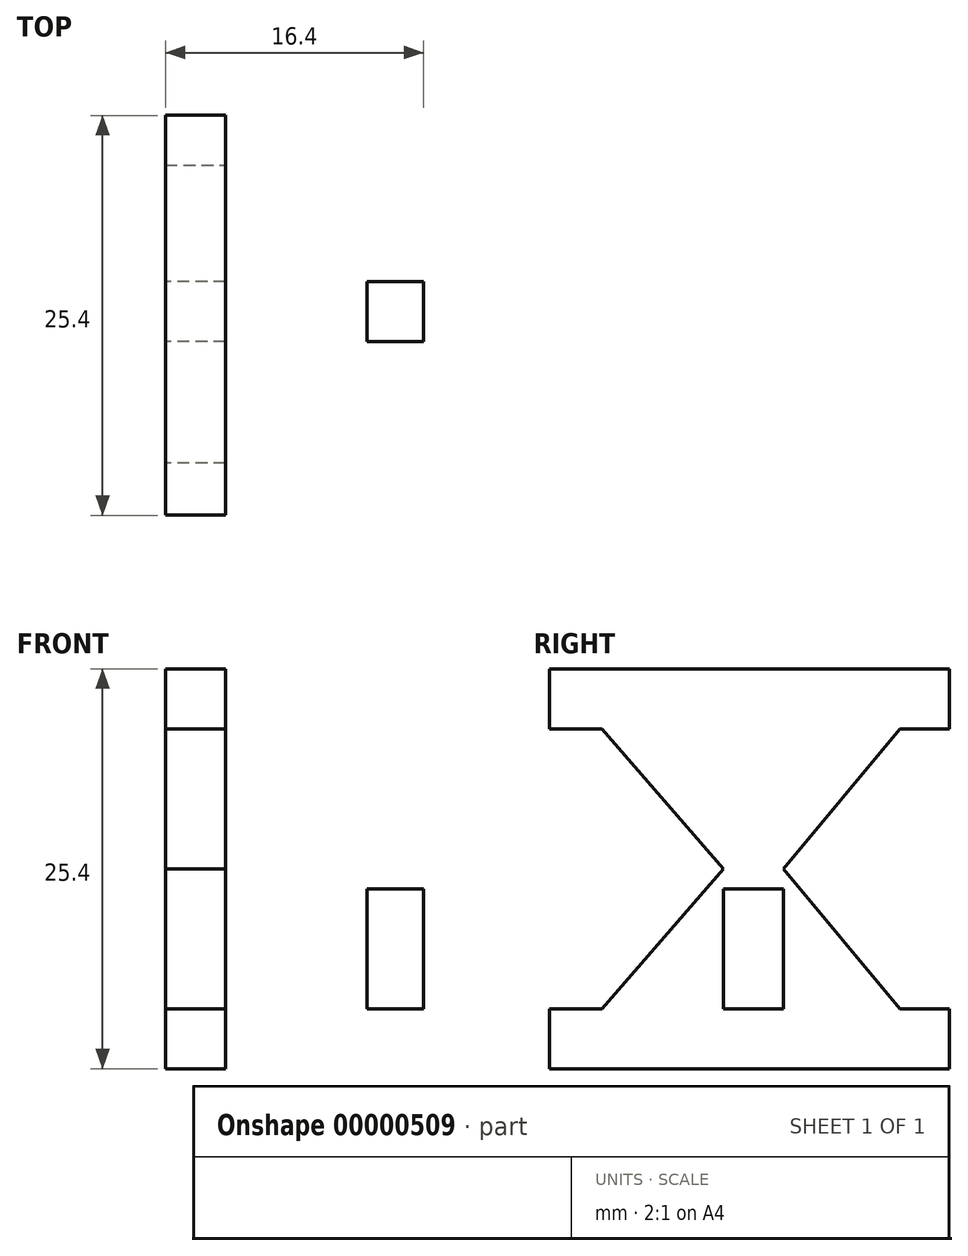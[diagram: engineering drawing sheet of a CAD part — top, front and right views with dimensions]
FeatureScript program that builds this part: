
annotation { "Feature Type Name" : "Feature", "Feature Type Description" : "" }
export const myFeature = defineFeature(function(context is Context, id is Id, definition is map)
    precondition{}
    {
        {
            var Q0;
            Q0=qCreatedBy(makeId("Top.planeOp"),FACE);
            var sketch = newSketch(context, id + "F0", { "sketchPlane" : qUnion([Q0])});
            skLineSegment(sketch, "E0.bottom", {"start": v(0, 12.45) * mm, "end": v(-3.81, 12.45) * mm});
            skLineSegment(sketch, "E0.top", {"start": v(0, -12.95) * mm, "end": v(-3.8, -12.95) * mm});
            skLineSegment(sketch, "E0.left", {"start": v(0, 12.45) * mm, "end": v(0, -12.95) * mm});
            skLineSegment(sketch, "E0.right", {"start": v(-3.81, 12.45) * mm, "end": v(-3.8, -12.95) * mm});
            skArc(sketch, "E1", {"start": v(0, -12.95) * mm, "mid": v(12.7, -0.25) * mm, "end": v(0, 12.45) * mm});
            skLineSegment(sketch, "E2", {"start": v(0, 12.45) * mm, "end": v(0, 8.64) * mm});
            skLineSegment(sketch, "E3", {"start": v(0, 8.64) * mm, "end": v(0, -9.14) * mm});
            skLineSegment(sketch, "E4", {"start": v(0, -9.14) * mm, "end": v(0, -12.95) * mm});
            skLineSegment(sketch, "E5", {"start": v(0, 0) * mm, "end": v(8.89, 0) * mm});
            skLineSegment(sketch, "E6", {"start": v(8.89, 0) * mm, "end": v(12.7, 0) * mm});
            skArc(sketch, "E7", {"start": v(0, -9.14) * mm, "mid": v(8.9, -0.25) * mm, "end": v(0, 8.64) * mm});
            skSolve(sketch);
        }
        {
            var Q0;
            Q0=makeQuery(id+"F0.imprint","IMPRINT",FACE,{"disambiguationData":[TD([[makeQuery(id+"F0.imprint","IMPRINT",EDGE,{"derivedFrom":sQuery(id+"F0.wireOp",EDGE,"E0.bottom")}),1.0]])]});
            var Q1;
            {var subQ2=sQuery(id+"F0.wireOp",EDGE,"E4");Q1=makeQuery(id+"F0.imprint","IMPRINT",FACE,{"disambiguationData":[TD([[makeQuery(id+"F0.imprint","IMPRINT",EDGE,{"derivedFrom":subQ2}),1.0]])]});}
            var Q2;
            {var subQ2=sQuery(id+"F0.wireOp",EDGE,"E2");Q2=makeQuery(id+"F0.imprint","IMPRINT",FACE,{"disambiguationData":[TD([[makeQuery(id+"F0.imprint","IMPRINT",EDGE,{"derivedFrom":subQ2}),1.0]])]});}
            extrude(context, id + "F1", {"entities" : qUnion([Q0, Q1, Q2]), "depth" : 3.8 * mm});
        }
        {
            var Q0;
            Q0=makeQuery(id+"F1.opExtrude","CAP_FACE",FACE,{"disambiguationData":[OSD([sQuery(id+"F0.wireOp",EDGE,"E0.bottom"),sQuery(id+"F0.wireOp",EDGE,"E0.top"),sQuery(id+"F0.wireOp",EDGE,"E0.right"),sQuery(id+"F0.wireOp",EDGE,"E1"),sQuery(id+"F0.wireOp",EDGE,"E3"),sQuery(id+"F0.wireOp",EDGE,"E7")])],"isStart":false});
            var sketch = newSketch(context, id + "F2", { "sketchPlane" : qUnion([Q0])});
            skLineSegment(sketch, "E8", {"start": v(0, 0) * mm, "end": v(-3.8, 0) * mm, "construction": true});
            skLineSegment(sketch, "E9.rect.bottom", {"start": v(-3.8, -1.9) * mm, "end": v(0, -1.9) * mm});
            skLineSegment(sketch, "E9.rect.top", {"start": v(-3.8, 1.9) * mm, "end": v(0, 1.9) * mm});
            skLineSegment(sketch, "E9.rect.left", {"start": v(-3.8, -1.9) * mm, "end": v(-3.8, 1.9) * mm});
            skLineSegment(sketch, "E9.rect.right", {"start": v(0, -1.9) * mm, "end": v(0, 1.9) * mm});
            skPoint(sketch, "E9.rect.middle", {"position": v(-1.9, 0) * mm});
            skSolve(sketch);
        }
        {
            var Q0;
            Q0 = qSketchRegion(id + "F2", true);
            extrude(context, id + "F3", {"entities" : qUnion([Q0]), "operationType" : NewBodyOperationType.ADD, "depth" : 25.4 * mm - 7.62 * mm});
        }
        {
            var Q0;
            Q0=makeQuery(id+"F1.opExtrude","CAP_FACE",FACE,{"disambiguationData":[OSD([sQuery(id+"F0.wireOp",EDGE,"E0.bottom"),sQuery(id+"F0.wireOp",EDGE,"E0.top"),sQuery(id+"F0.wireOp",EDGE,"E0.right"),sQuery(id+"F0.wireOp",EDGE,"E1"),sQuery(id+"F0.wireOp",EDGE,"E3"),sQuery(id+"F0.wireOp",EDGE,"E7")])],"isStart":false});
            var sketch = newSketch(context, id + "F4", { "sketchPlane" : qUnion([Q0])});
            skLineSegment(sketch, "E10", {"start": v(12.7, 0) * mm, "end": v(8.89, 0) * mm, "construction": true});
            skLineSegment(sketch, "E11.rect.bottom", {"start": v(12.6, -1.9) * mm, "end": v(9, -1.9) * mm});
            skLineSegment(sketch, "E11.rect.top", {"start": v(12.6, 1.9) * mm, "end": v(9, 1.9) * mm});
            skLineSegment(sketch, "E11.rect.left", {"start": v(12.6, -1.9) * mm, "end": v(12.6, 1.9) * mm});
            skLineSegment(sketch, "E11.rect.right", {"start": v(9, -1.9) * mm, "end": v(9, 1.9) * mm});
            skPoint(sketch, "E11.rect.middle", {"position": v(10.8, 0) * mm});
            skSolve(sketch);
        }
        {
            var Q0;
            Q0 = qSketchRegion(id + "F4", true);
            extrude(context, id + "F5", {"entities" : qUnion([Q0]), "operationType" : NewBodyOperationType.ADD, "depth" : 7.62 * mm});
        }
        {
            var Q0;
            Q0=makeQuery(id+"F3.opExtrude","CAP_FACE",FACE,{"disambiguationData":[OSD([sQuery(id+"F2.wireOp",EDGE,"E9.rect.bottom"),sQuery(id+"F2.wireOp",EDGE,"E9.rect.top"),sQuery(id+"F2.wireOp",EDGE,"E9.rect.left"),sQuery(id+"F2.wireOp",EDGE,"E9.rect.right")])],"isStart":false});
            extrude(context, id + "F6", {"entities" : qUnion([Q0]), "operationType" : NewBodyOperationType.ADD, "depth" : 3.8 * mm});
        }
        {
            var Q0;
            {var subQ0=sQuery(id+"F2.wireOp",EDGE,"E9.rect.bottom");Q0=makeQuery(id+"F6.boolean.opBoolean","MERGE",FACE,{"derivedFrom":[makeQuery(id+"F3.opExtrude","SWEPT_FACE",FACE,{"disambiguationData":[OSD([subQ0])]}),makeQuery(id+"F6.opExtrude","SWEPT_FACE",FACE,{"disambiguationData":[OSD([subQ0])]})]});}
            var sketch = newSketch(context, id + "F7", { "sketchPlane" : qUnion([Q0])});
            skLineSegment(sketch, "E12.bottom", {"start": v(-3.8, 25.4) * mm, "end": v(0, 25.4) * mm});
            skLineSegment(sketch, "E12.top", {"start": v(-3.8, 21.6) * mm, "end": v(0, 21.6) * mm});
            skLineSegment(sketch, "E12.left", {"start": v(-3.8, 25.4) * mm, "end": v(-3.8, 21.6) * mm});
            skLineSegment(sketch, "E12.right", {"start": v(0, 25.4) * mm, "end": v(0, 21.6) * mm});
            skSolve(sketch);
        }
        {
            var Q0;
            Q0=makeQuery(id+"F7.imprint","IMPRINT",FACE,{"disambiguationData":[TD([[makeQuery(id+"F7.imprint","IMPRINT",EDGE,{"derivedFrom":sQuery(id+"F7.wireOp",EDGE,"E12.bottom")}),-1.0]])]});
            var Q1;
            Q1=makeQuery(id+"F1.opExtrude","SWEPT_FACE",FACE,{"disambiguationData":[OSD([sQuery(id+"F0.wireOp",EDGE,"E0.top")])]});
            extrude(context, id + "F8", {"entities" : qUnion([Q0]), "operationType" : NewBodyOperationType.ADD, "endBound" : BoundingType.UP_TO_SURFACE, "endBoundEntityFace" : qUnion([Q1]), "depth" : 25.4 * mm});
        }
        {
            var Q0;
            Q0 = qSketchRegion(id + "F7", true);
            var Q1;
            Q1=makeQuery(id+"F1.opExtrude","SWEPT_FACE",FACE,{"disambiguationData":[OSD([sQuery(id+"F0.wireOp",EDGE,"E0.bottom")])]});
            extrude(context, id + "F9", {"entities" : qUnion([Q0]), "operationType" : NewBodyOperationType.ADD, "endBound" : BoundingType.UP_TO_SURFACE, "oppositeDirection" : true, "endBoundEntityFace" : qUnion([Q1]), "depth" : 25.4 * mm});
        }
        {
            var Q0;
            {var subQ0=sQuery(id+"F2.wireOp",EDGE,"E9.rect.left");var subQ1=sQuery(id+"F7.wireOp",EDGE,"E12.left");Q0=makeQuery(id+"F9.boolean.opBoolean","MERGE",FACE,{"derivedFrom":[makeQuery(id+"F8.boolean.opBoolean","MERGE",FACE,{"derivedFrom":[makeQuery(id+"F6.boolean.opBoolean","MERGE",FACE,{"derivedFrom":[makeQuery(id+"F3.boolean.opBoolean","MERGE",FACE,{"derivedFrom":[makeQuery(id+"F1.opExtrude","SWEPT_FACE",FACE,{"disambiguationData":[OSD([sQuery(id+"F0.wireOp",EDGE,"E0.right")])]}),makeQuery(id+"F3.opExtrude","SWEPT_FACE",FACE,{"disambiguationData":[OSD([subQ0])]})]}),makeQuery(id+"F6.opExtrude","SWEPT_FACE",FACE,{"disambiguationData":[OSD([subQ0])]})]}),makeQuery(id+"F8.opExtrude","SWEPT_FACE",FACE,{"disambiguationData":[OSD([subQ1])]})]}),makeQuery(id+"F9.opExtrude","SWEPT_FACE",FACE,{"disambiguationData":[OSD([subQ1])]})]});}
            var sketch = newSketch(context, id + "F10", { "sketchPlane" : qUnion([Q0])});
            skLineSegment(sketch, "E13", {"start": v(0, 25.4) * mm, "end": v(0, 0) * mm, "construction": true});
            skLineSegment(sketch, "E14", {"start": v(-1.9, 12.7) * mm, "end": v(-12.45, 25.4) * mm});
            skLineSegment(sketch, "E15", {"start": v(-12.45, 0) * mm, "end": v(-1.9, 12.7) * mm});
            skLineSegment(sketch, "E16", {"start": v(12.95, 0) * mm, "end": v(1.9, 12.7) * mm});
            skLineSegment(sketch, "E17", {"start": v(12.95, 25.4) * mm, "end": v(1.9, 12.7) * mm});
            skLineSegment(sketch, "E18", {"start": v(12.95, 0) * mm, "end": v(-12.45, 0) * mm});
            skLineSegment(sketch, "E19", {"start": v(12.95, 25.4) * mm, "end": v(-12.45, 25.4) * mm});
            skSolve(sketch);
        }
        {
            var Q0;
            Q0 = qSketchRegion(id + "F10", true);
            var Q1;
            {var subQ0=sQuery(id+"F2.wireOp",EDGE,"E9.rect.right");var subQ1=sQuery(id+"F7.wireOp",EDGE,"E12.right");Q1=makeQuery(id+"F9.boolean.opBoolean","MERGE",FACE,{"derivedFrom":[makeQuery(id+"F8.boolean.opBoolean","MERGE",FACE,{"derivedFrom":[makeQuery(id+"F6.boolean.opBoolean","MERGE",FACE,{"derivedFrom":[makeQuery(id+"F3.boolean.opBoolean","MERGE",FACE,{"derivedFrom":[makeQuery(id+"F1.opExtrude","SWEPT_FACE",FACE,{"disambiguationData":[OSD([sQuery(id+"F0.wireOp",EDGE,"E3")])]}),makeQuery(id+"F3.opExtrude","SWEPT_FACE",FACE,{"disambiguationData":[OSD([subQ0])]})]}),makeQuery(id+"F6.opExtrude","SWEPT_FACE",FACE,{"disambiguationData":[OSD([subQ0])]})]}),makeQuery(id+"F8.opExtrude","SWEPT_FACE",FACE,{"disambiguationData":[OSD([subQ1])]})]}),makeQuery(id+"F9.opExtrude","SWEPT_FACE",FACE,{"disambiguationData":[OSD([subQ1])]})]});}
            extrude(context, id + "F11", {"entities" : qUnion([Q0]), "operationType" : NewBodyOperationType.ADD, "endBound" : BoundingType.UP_TO_SURFACE, "oppositeDirection" : true, "endBoundEntityFace" : qUnion([Q1]), "depth" : 25.4 * mm});
        }
    });
